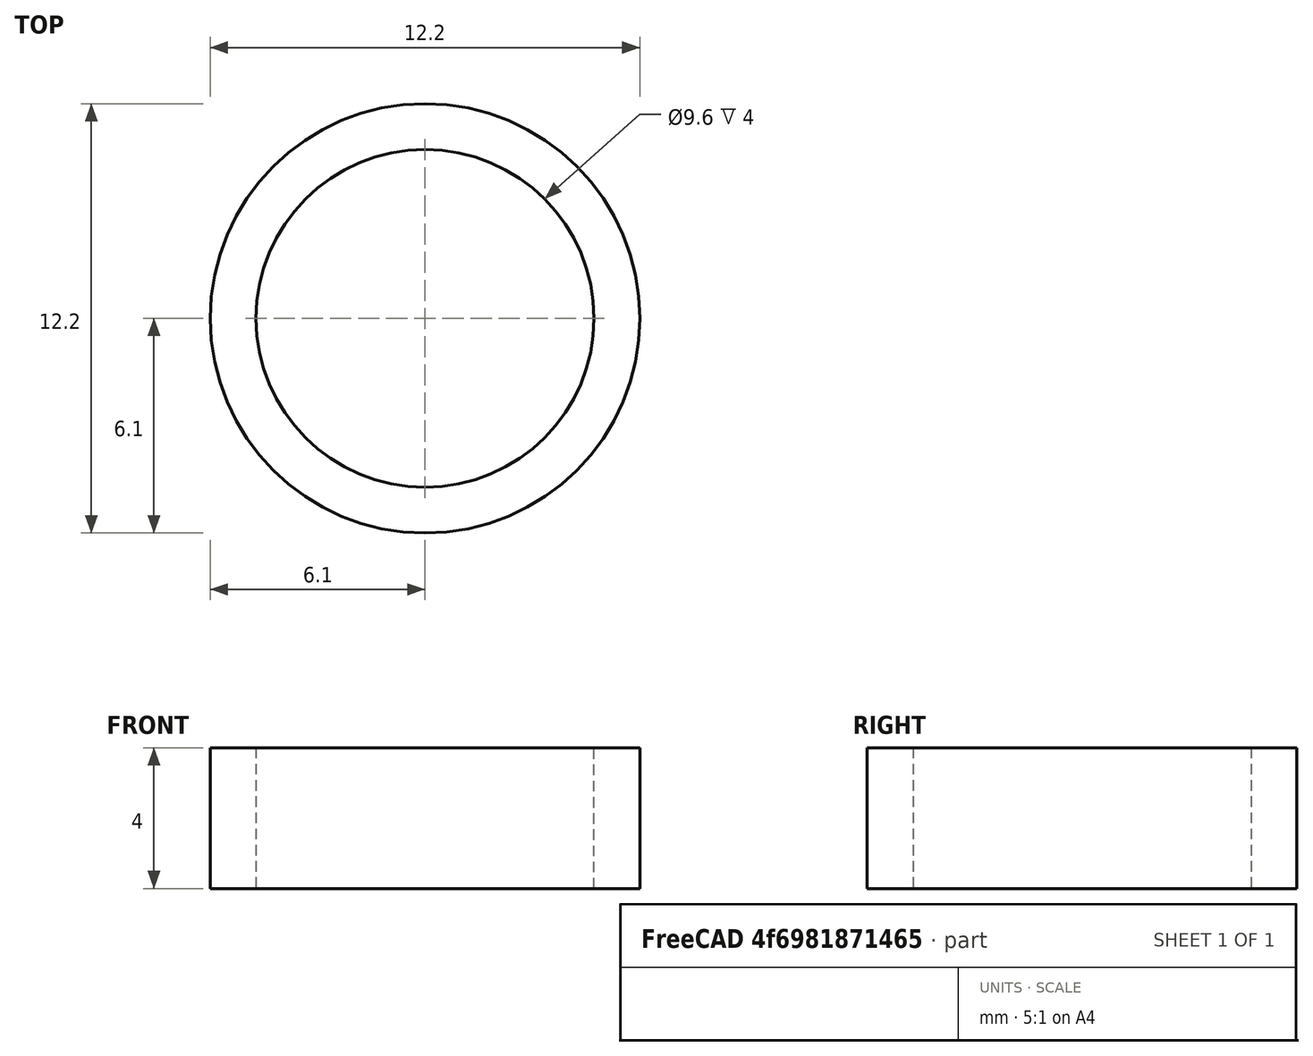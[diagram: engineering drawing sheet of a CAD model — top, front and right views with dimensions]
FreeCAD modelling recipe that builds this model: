
FCSTD DOCUMENT  (FreeCAD 0.21R33771 (Git))
Label: arruela-espacadora-ponta
License: All rights reserved
LicenseURL: https://en.wikipedia.org/wiki/All_rights_reserved
objects: Sketcher::SketchObject×1, PartDesign::Pad×1, PartDesign::Body×1
note: 4 computed .brp shape members not serialized (recipe doc carries the construction recipe); baked Part::Feature solids carry a one-line shape summary decoded from their .brp

FEATURE [Sketcher::SketchObject] Sketch
  FullyConstrained = true
  MapMode = 5
  Support = -> [XY_Plane]
  sketch-geometry (2):
    g0: Circle CenterX=0 CenterY=0 CenterZ=0 NormalX=0 NormalY=0 NormalZ=1 AngleXU=0 Radius=4.8
    g1: Circle CenterX=0 CenterY=0 CenterZ=0 NormalX=0 NormalY=0 NormalZ=1 AngleXU=0 Radius=6.1
  constraints (4):
    c: Coincident(g0,g-1)
    c: Coincident(g1,g0)
    c: Diameter(g0) = 9.6
    c: Diameter(g1) = 12.2
FEATURE [PartDesign::Pad] Pad
  Direction = (0,0,1)
  Length = 4
  Length2 = 10
  Profile = -> Sketch
  ReferenceAxis = -> Sketch [N_Axis]
  Type = 0
FEATURE [PartDesign::Body] Body
  Group = -> [Sketch,Pad]
  Origin = -> Origin
  Tip = -> Pad
